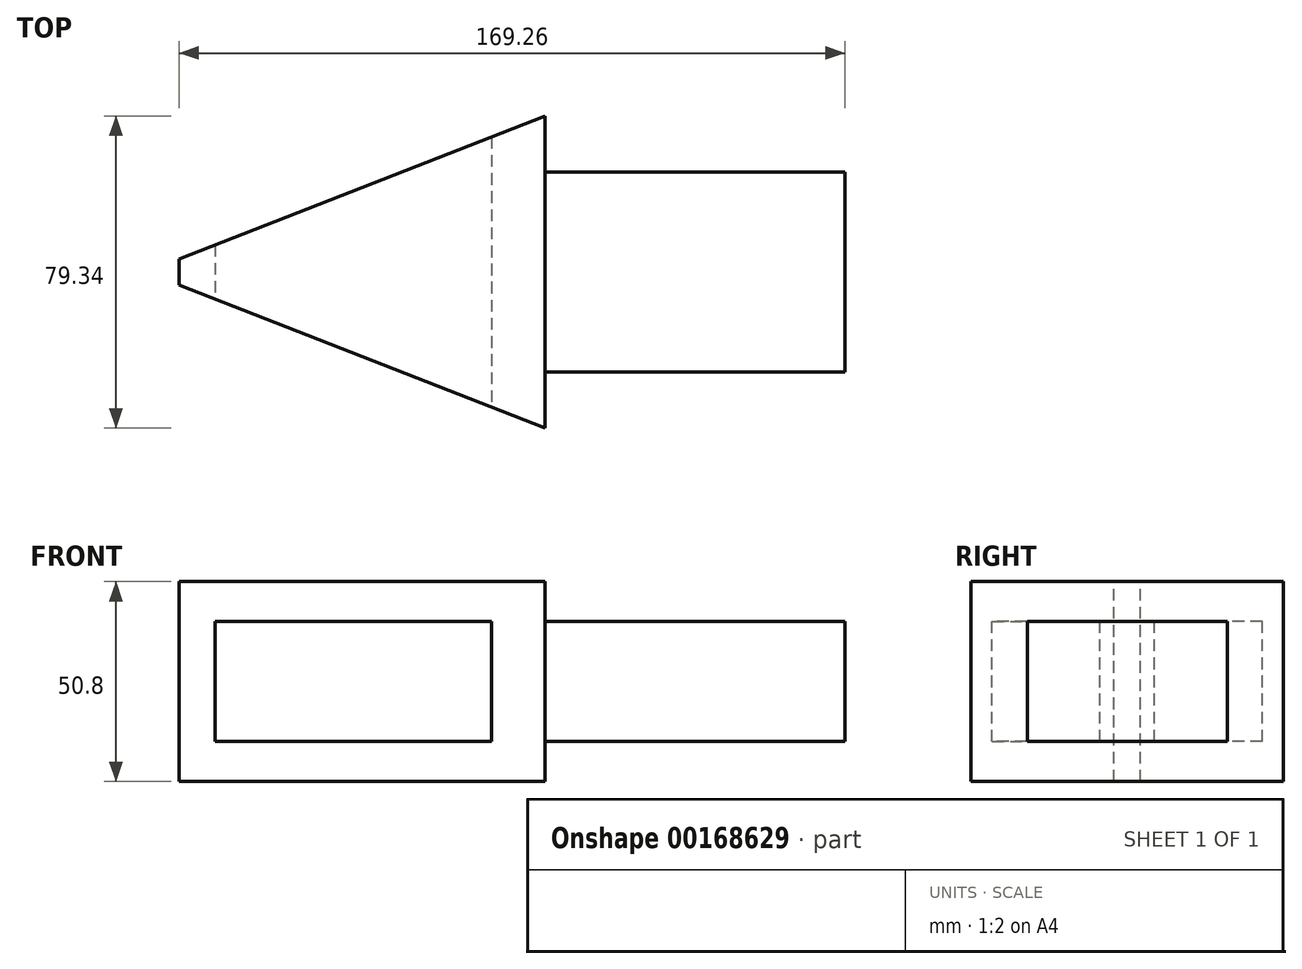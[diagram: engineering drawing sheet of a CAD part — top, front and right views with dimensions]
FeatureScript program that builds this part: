
annotation { "Feature Type Name" : "Feature", "Feature Type Description" : "" }
export const myFeature = defineFeature(function(context is Context, id is Id, definition is map)
    precondition{}
    {
        {
            var Q0;
            Q0=qCreatedBy(makeId("Top.planeOp"),FACE);
            var sketch = newSketch(context, id + "F0", { "sketchPlane" : qUnion([Q0])});
            skLineSegment(sketch, "E0", {"start": v(0, 39.67) * mm, "end": v(0, -36.53) * mm});
            skLineSegment(sketch, "E1", {"start": v(0, -36.53) * mm, "end": v(-101.6, 0) * mm});
            skLineSegment(sketch, "E2", {"start": v(-101.6, 0) * mm, "end": v(0, 39.67) * mm});
            skSolve(sketch);
        }
        {
            var Q0;
            Q0 = qSketchRegion(id + "F0", true);
            extrude(context, id + "F1", {"entities" : qUnion([Q0]), "endBound" : BoundingType.SYMMETRIC, "depth" : 50.8 * mm});
        }
        {
            var Q0;
            Q0=qCreatedBy(makeId("Front.planeOp"),FACE);
            var sketch = newSketch(context, id + "F2", { "sketchPlane" : qUnion([Q0])});
            skLineSegment(sketch, "E3.bottom", {"start": v(-83.82, 15.24) * mm, "end": v(-13.68, 15.24) * mm});
            skLineSegment(sketch, "E3.top", {"start": v(-83.82, -15.24) * mm, "end": v(-13.68, -15.24) * mm});
            skLineSegment(sketch, "E3.left", {"start": v(-83.82, 15.24) * mm, "end": v(-83.82, -15.24) * mm});
            skLineSegment(sketch, "E3.right", {"start": v(-13.68, 15.24) * mm, "end": v(-13.68, -15.24) * mm});
            skSolve(sketch);
        }
        {
            var Q0;
            Q0 = qSketchRegion(id + "F2", true);
            extrude(context, id + "F3", {"entities" : qUnion([Q0]), "operationType" : NewBodyOperationType.REMOVE, "endBound" : BoundingType.SYMMETRIC, "oppositeDirection" : true, "depth" : 127 * mm});
        }
        {
            var Q0;
            Q0=qCreatedBy(makeId("Top.planeOp"),FACE);
            var sketch = newSketch(context, id + "F4", { "sketchPlane" : qUnion([Q0])});
            skLineSegment(sketch, "E4", {"start": v(-101.6, 0) * mm, "end": v(-93.06, 3.33) * mm});
            skLineSegment(sketch, "E5", {"start": v(-93.06, 3.33) * mm, "end": v(-93.06, -3.07) * mm});
            skLineSegment(sketch, "E6", {"start": v(-93.06, -3.07) * mm, "end": v(-101.6, 0) * mm});
            skSolve(sketch);
        }
        {
            var Q0;
            Q0 = qSketchRegion(id + "F4", true);
            extrude(context, id + "F5", {"entities" : qUnion([Q0]), "operationType" : NewBodyOperationType.REMOVE, "endBound" : BoundingType.SYMMETRIC, "oppositeDirection" : true, "depth" : 50.8 * mm});
        }
        {
            var Q0;
            Q0=qCreatedBy(makeId("Top.planeOp"),FACE);
            var sketch = newSketch(context, id + "F6", { "sketchPlane" : qUnion([Q0])});
            skLineSegment(sketch, "E7.bottom", {"start": v(0, 0) * mm, "end": v(76.2, 0) * mm});
            skLineSegment(sketch, "E7.top", {"start": v(0, 25.4) * mm, "end": v(76.2, 25.4) * mm});
            skLineSegment(sketch, "E7.left", {"start": v(0, 0) * mm, "end": v(0, 25.4) * mm});
            skLineSegment(sketch, "E7.right", {"start": v(76.2, 0) * mm, "end": v(76.2, 25.4) * mm});
            skSolve(sketch);
        }
        {
            var Q0;
            Q0 = qSketchRegion(id + "F6", true);
            extrude(context, id + "F7", {"entities" : qUnion([Q0]), "operationType" : NewBodyOperationType.ADD, "endBound" : BoundingType.SYMMETRIC, "depth" : 30.48 * mm});
        }
        {
            var Q0;
            Q0=makeQuery(id+"F1.opExtrude","SWEPT_BODY",BODY,{"disambiguationData":[OSD([sQuery(id+"F0.wireOp",EDGE,"E0"),sQuery(id+"F0.wireOp",EDGE,"E1"),sQuery(id+"F0.wireOp",EDGE,"E2")])]});
            var Q1;
            Q1=qCreatedBy(makeId("Front.planeOp"),FACE);
            mirror(context, id + "F8", {"operationType" : NewBodyOperationType.ADD, "entities" : qUnion([Q0]), "mirrorPlane" : qUnion([Q1])});
        }
    });
